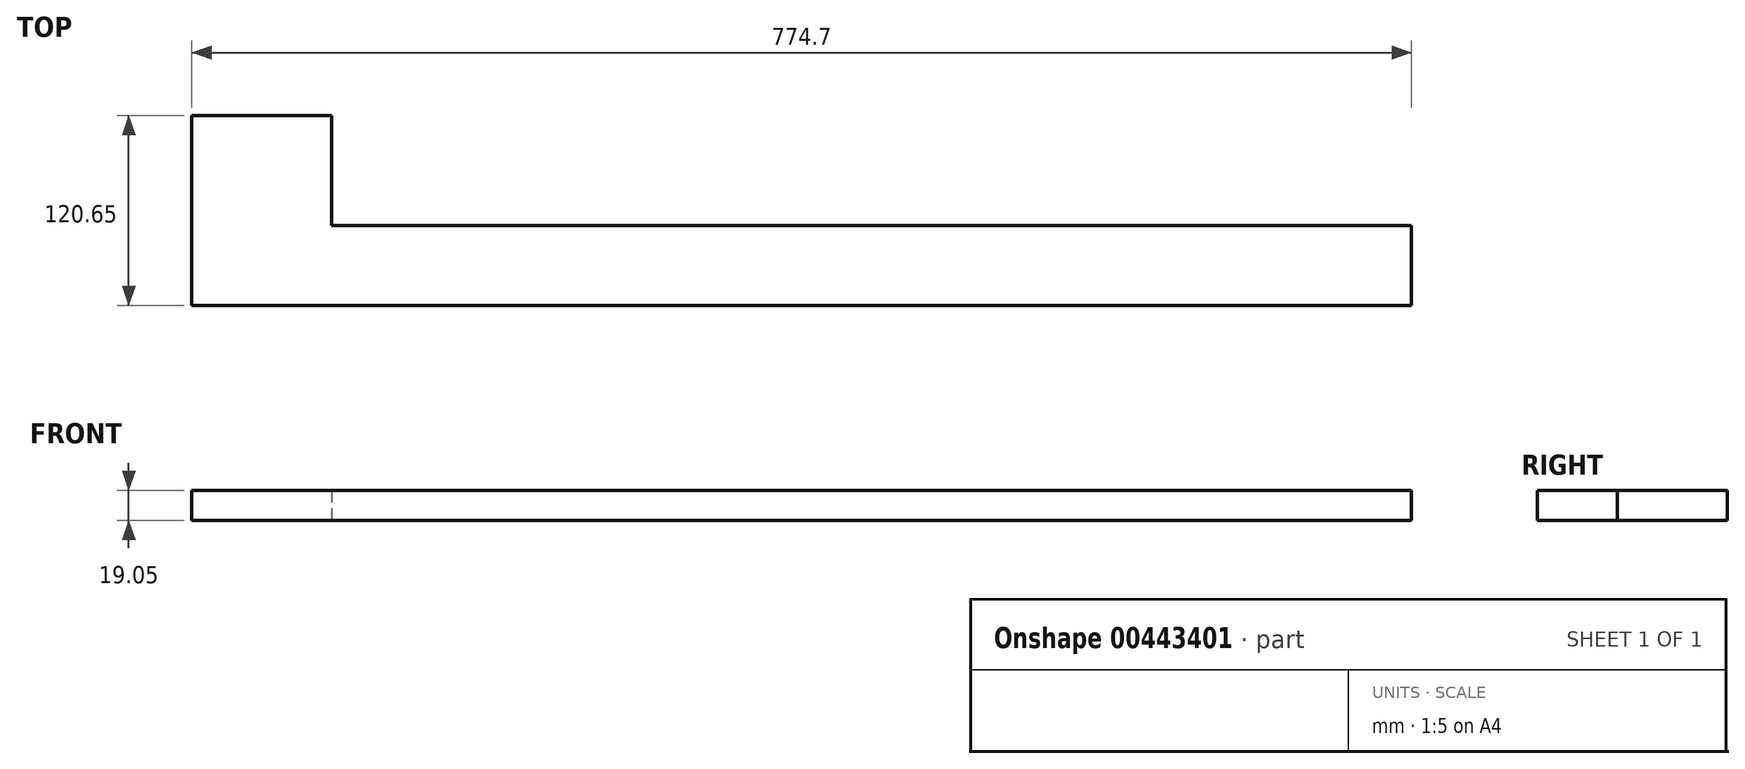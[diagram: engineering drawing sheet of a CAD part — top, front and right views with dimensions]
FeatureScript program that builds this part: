
annotation { "Feature Type Name" : "Feature", "Feature Type Description" : "" }
export const myFeature = defineFeature(function(context is Context, id is Id, definition is map)
    precondition{}
    {
        {
            var Q0;
            Q0=qCreatedBy(makeId("Top.planeOp"),FACE);
            var sketch = newSketch(context, id + "F0", { "sketchPlane" : qUnion([Q0])});
            skLineSegment(sketch, "E0", {"start": v(-310.75, 0) * mm, "end": v(463.95, 0) * mm});
            skLineSegment(sketch, "E1", {"start": v(463.95, 0) * mm, "end": v(463.95, 50.8) * mm});
            skLineSegment(sketch, "E2", {"start": v(463.95, 50.8) * mm, "end": v(-221.85, 50.8) * mm});
            skLineSegment(sketch, "E3", {"start": v(-221.85, 50.8) * mm, "end": v(-221.85, 120.65) * mm});
            skLineSegment(sketch, "E4", {"start": v(-221.85, 120.65) * mm, "end": v(-310.75, 120.65) * mm});
            skLineSegment(sketch, "E5", {"start": v(-310.75, 120.65) * mm, "end": v(-310.75, 0) * mm});
            skSolve(sketch);
        }
        {
            var Q0;
            Q0=qSketchRegion(id+"F0",true);
            extrude(context, id + "F1", {"entities" : qUnion([Q0]), "depth" : 19.05 * mm});
        }
    });
